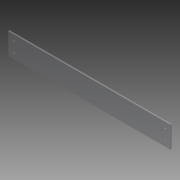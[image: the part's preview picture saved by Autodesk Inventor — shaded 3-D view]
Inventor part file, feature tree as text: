
AUTODESK INVENTOR PART (.ipt)
format: ipt  version: 2014 (Build 180170000, 170)  size: 79,872 bytes
history: native  units: in
note: dims shown in document units (in); Inventor stores cm internally (conversion verified against a paired STEP export)
features: extrude x1, sketch x1
ambient origin geometry x8: Origin, YZ Plane, XZ Plane, XY Plane, X Axis, Y Axis, Z Axis, Center Point
bodies: Solid1 (feature_tree)
feature tree (2):
  extrude  "Extrusion1"  Depth=15.0in
  sketch  "Sketch1"  dims[d0=2.0in d1=15.0in d2=0.163in d3=0.5in d4=0.5in d5=0.7874in d7=1.0in d8=0.7874in d10=14.0in d13=0.125in d14=0.0in]
